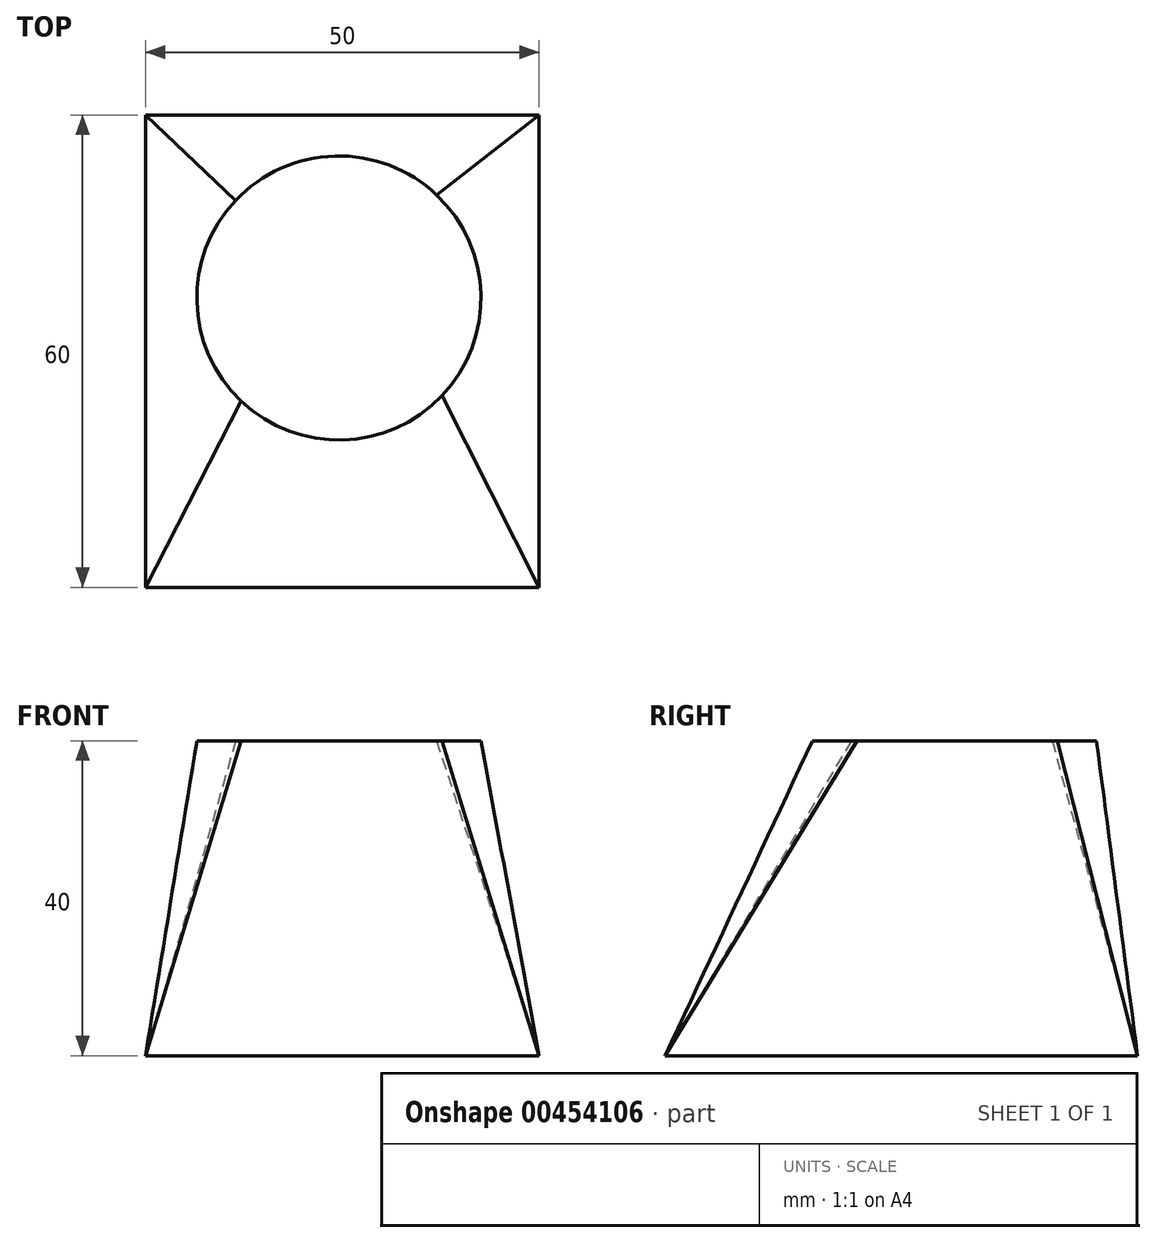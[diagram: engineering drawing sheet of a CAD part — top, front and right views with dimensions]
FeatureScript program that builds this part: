
annotation { "Feature Type Name" : "Feature", "Feature Type Description" : "" }
export const myFeature = defineFeature(function(context is Context, id is Id, definition is map)
    precondition{}
    {
        {
            var Q0;
            Q0=qCreatedBy(makeId("Top.planeOp"),FACE);
            var sketch = newSketch(context, id + "F0", { "sketchPlane" : qUnion([Q0])});
            skLineSegment(sketch, "E0.bottom", {"start": v(0, 0) * mm, "end": v(50, 0) * mm});
            skLineSegment(sketch, "E0.top", {"start": v(0, -60) * mm, "end": v(50, -60) * mm});
            skLineSegment(sketch, "E0.left", {"start": v(0, 0) * mm, "end": v(0, -60) * mm});
            skLineSegment(sketch, "E0.right", {"start": v(50, 0) * mm, "end": v(50, -60) * mm});
            skSolve(sketch);
        }
        {
            var Q0;
            Q0=qCreatedBy(makeId("Top.planeOp"),FACE);
            cPlane(context, id + "F1", {"entities" : qUnion([Q0]), "cplaneType" : CPlaneType.OFFSET, "offset" : 40 * mm, "width" : 150 * mm, "height" : 150 * mm});
        }
        {
            var Q0;
            Q0=qCreatedBy(id+"F1.planeOp",FACE);
            var sketch = newSketch(context, id + "F2", { "sketchPlane" : qUnion([Q0])});
            skCircle(sketch, "E1", {"center": v(24.55, -23.25) * mm, "radius": 18.05 * mm});
            skPoint(sketch, "E1.first.point", {"position": v(8.96, -14.17) * mm});
            skPoint(sketch, "E1.second.point", {"position": v(34.31, -38.43) * mm});
            skPoint(sketch, "E1.third.point", {"position": v(42.53, -21.65) * mm});
            skSolve(sketch);
        }
        {
            var Q0;
            Q0=makeQuery(id+"F2.imprint","IMPRINT",FACE,{"disambiguationData":[TD([[makeQuery(id+"F2.imprint","IMPRINT",EDGE,{"derivedFrom":sQuery(id+"F2.wireOp",EDGE,"E1")}),1.0]])]});
            var Q1;
            Q1=makeQuery(id+"F0.imprint","IMPRINT",FACE,{"disambiguationData":[TD([[makeQuery(id+"F0.imprint","IMPRINT",EDGE,{"derivedFrom":sQuery(id+"F0.wireOp",EDGE,"E0.bottom")}),-1.0]])]});
            loft(context, id + "F3", {"sheetProfilesArray" : [{ "sheetProfileEntities" : qUnion([Q0]) }, { "sheetProfileEntities" : qUnion([Q1]) }]});
        }
    });
